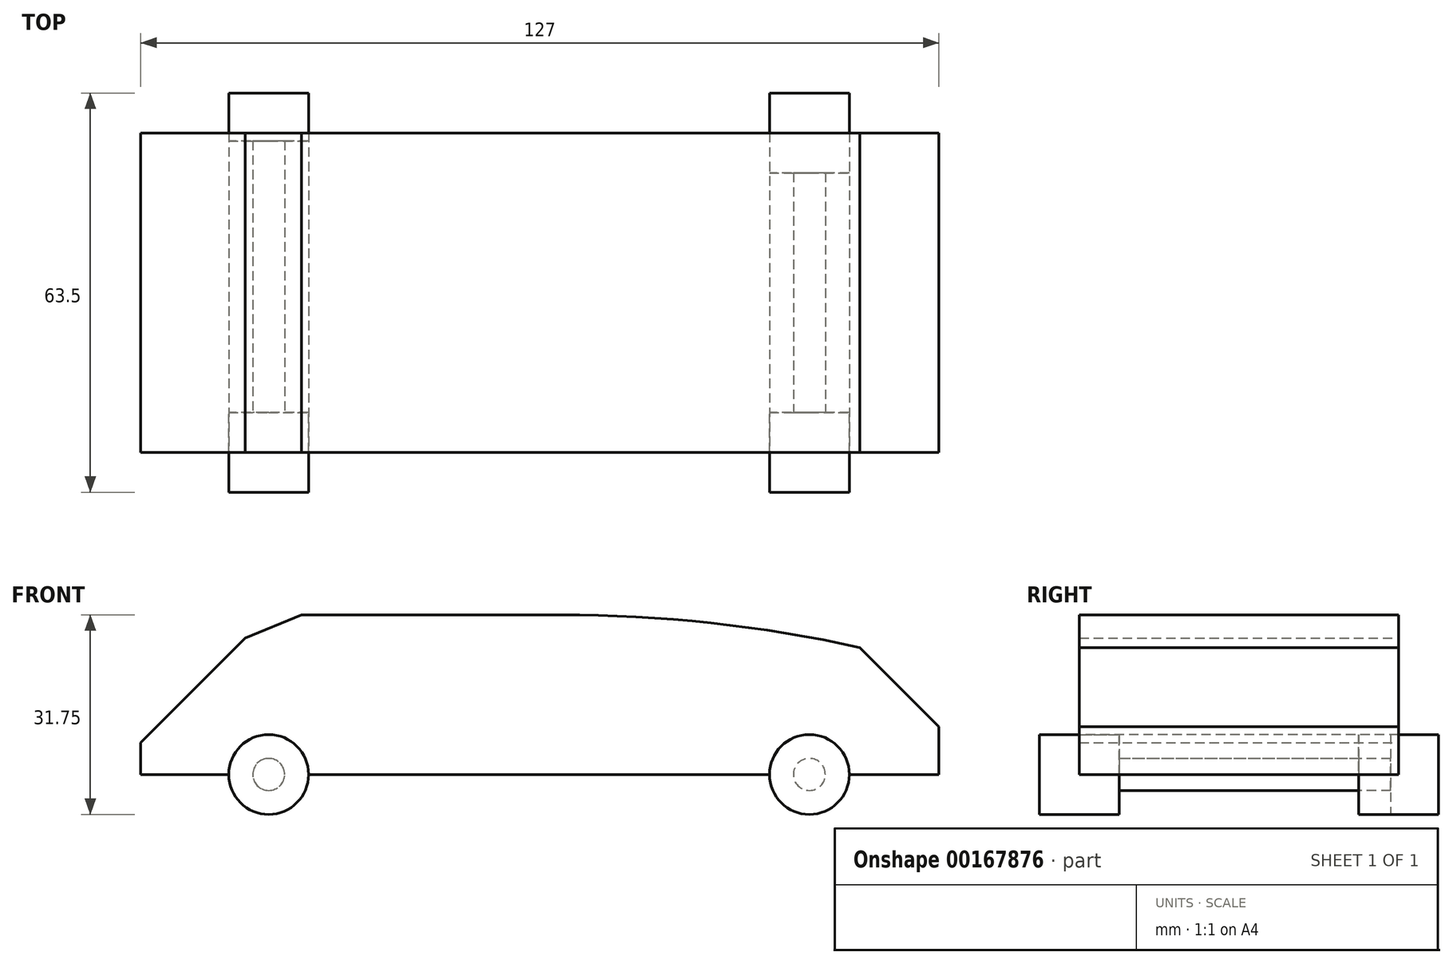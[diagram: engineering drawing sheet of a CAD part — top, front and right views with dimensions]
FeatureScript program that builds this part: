
annotation { "Feature Type Name" : "Feature", "Feature Type Description" : "" }
export const myFeature = defineFeature(function(context is Context, id is Id, definition is map)
    precondition{}
    {
        {
            var Q0;
            Q0=qCreatedBy(makeId("Top.planeOp"),FACE);
            var sketch = newSketch(context, id + "F0", { "sketchPlane" : qUnion([Q0])});
            skLineSegment(sketch, "E0.bottom", {"start": v(-59.82, 13.49) * mm, "end": v(67.18, 13.49) * mm});
            skLineSegment(sketch, "E0.top", {"start": v(-59.82, -37.31) * mm, "end": v(67.18, -37.31) * mm});
            skLineSegment(sketch, "E0.left", {"start": v(-59.82, 13.49) * mm, "end": v(-59.82, -37.31) * mm});
            skLineSegment(sketch, "E0.right", {"start": v(67.18, 13.49) * mm, "end": v(67.18, -37.31) * mm});
            skSolve(sketch);
        }
        {
            var Q0;
            Q0=makeQuery(id+"F0.imprint","IMPRINT",FACE,{"disambiguationData":[TD([[makeQuery(id+"F0.imprint","IMPRINT",EDGE,{"derivedFrom":sQuery(id+"F0.wireOp",EDGE,"E0.bottom")}),-1.0]])]});
            extrude(context, id + "F1", {"entities" : qUnion([Q0]), "depth" : 25.4 * mm});
        }
        {
            var Q0;
            Q0=makeQuery(id+"F1.opExtrude","CAP_EDGE",EDGE,{"disambiguationData":[OSD([sQuery(id+"F0.wireOp",EDGE,"E0.right")])],"isStart":false});
            chamfer(context, id + "F2", {"entities" : qUnion([Q0]), "width" : 17.78 * mm, "tangentPropagation" : true});
        }
        {
            var Q0;
            {var subQ0=sQuery(id+"F0.wireOp",EDGE,"E0.right");Q0=makeQuery(id+"F2.opChamfer","BLEND_EDGE",EDGE,{"blendedFrom":[makeQuery(id+"F1.opExtrude","CAP_EDGE",EDGE,{"disambiguationData":[OSD([subQ0])],"isStart":false}),makeQuery(id+"F1.opExtrude","CAP_FACE",FACE,{"disambiguationData":[OSD([sQuery(id+"F0.wireOp",EDGE,"E0.bottom"),sQuery(id+"F0.wireOp",EDGE,"E0.top"),sQuery(id+"F0.wireOp",EDGE,"E0.left"),subQ0])],"isStart":false})],"blendedInto":[makeQuery(id+"F1.opExtrude","CAP_FACE",FACE,{"disambiguationData":[OSD([sQuery(id+"F0.wireOp",EDGE,"E0.bottom"),sQuery(id+"F0.wireOp",EDGE,"E0.top"),sQuery(id+"F0.wireOp",EDGE,"E0.left"),subQ0])],"isStart":false})]});}
            chamfer(context, id + "F3", {"entities" : qUnion([Q0]), "width" : 17.78 * mm, "tangentPropagation" : true});
        }
        {
            var Q0;
            {var subQ0=sQuery(id+"F0.wireOp",EDGE,"E0.right");var subQ1=makeQuery(id+"F1.opExtrude","CAP_FACE",FACE,{"disambiguationData":[OSD([sQuery(id+"F0.wireOp",EDGE,"E0.bottom"),sQuery(id+"F0.wireOp",EDGE,"E0.top"),sQuery(id+"F0.wireOp",EDGE,"E0.left"),subQ0])],"isStart":false});Q0=makeQuery(id+"F3.opChamfer","BLEND_EDGE",EDGE,{"blendedFrom":[makeQuery(id+"F2.opChamfer","BLEND_EDGE",EDGE,{"blendedFrom":[makeQuery(id+"F1.opExtrude","CAP_EDGE",EDGE,{"disambiguationData":[OSD([subQ0])],"isStart":false}),subQ1],"blendedInto":[subQ1]}),subQ1],"blendedInto":[subQ1]});}
            fillet(context, id + "F4", {"entities" : qUnion([Q0]), "radius" : 220.4 * mm, "tangentPropagation" : true, "allowEdgeOverflow" : false});
        }
        {
            var Q0;
            Q0=makeQuery(id+"F1.opExtrude","CAP_EDGE",EDGE,{"disambiguationData":[OSD([sQuery(id+"F0.wireOp",EDGE,"E0.left")])],"isStart":false});
            chamfer(context, id + "F5", {"entities" : qUnion([Q0]), "width" : 20.32 * mm, "tangentPropagation" : true});
        }
        {
            var Q0;
            {var subQ0=sQuery(id+"F0.wireOp",EDGE,"E0.left");Q0=makeQuery(id+"F5.opChamfer","BLEND_EDGE",EDGE,{"blendedFrom":[makeQuery(id+"F1.opExtrude","CAP_EDGE",EDGE,{"disambiguationData":[OSD([subQ0])],"isStart":false}),makeQuery(id+"F1.opExtrude","CAP_FACE",FACE,{"disambiguationData":[OSD([sQuery(id+"F0.wireOp",EDGE,"E0.bottom"),sQuery(id+"F0.wireOp",EDGE,"E0.top"),subQ0,sQuery(id+"F0.wireOp",EDGE,"E0.right")])],"isStart":false})],"blendedInto":[makeQuery(id+"F1.opExtrude","CAP_FACE",FACE,{"disambiguationData":[OSD([sQuery(id+"F0.wireOp",EDGE,"E0.bottom"),sQuery(id+"F0.wireOp",EDGE,"E0.top"),subQ0,sQuery(id+"F0.wireOp",EDGE,"E0.right")])],"isStart":false})]});}
            chamfer(context, id + "F6", {"entities" : qUnion([Q0]), "width" : 12.7 * mm, "tangentPropagation" : true});
        }
        {
            var Q0;
            Q0=makeQuery(id+"F1.opExtrude","SWEPT_FACE",FACE,{"disambiguationData":[OSD([sQuery(id+"F0.wireOp",EDGE,"E0.top")])]});
            var sketch = newSketch(context, id + "F7", { "sketchPlane" : qUnion([Q0])});
            skCircle(sketch, "E1", {"center": v(-39.47, 0) * mm, "radius": 6.35 * mm});
            skCircle(sketch, "E2", {"center": v(46.57, 0) * mm, "radius": 6.35 * mm});
            skSolve(sketch);
        }
        {
            var Q0;
            Q0=makeQuery(id+"F1.opExtrude","SWEPT_FACE",FACE,{"disambiguationData":[OSD([sQuery(id+"F0.wireOp",EDGE,"E0.bottom")])]});
            var sketch = newSketch(context, id + "F8", { "sketchPlane" : qUnion([Q0])});
            skCircle(sketch, "E3.0", {"center": v(-46.57, 0) * mm, "radius": 6.35 * mm});
            skCircle(sketch, "E3.1", {"center": v(39.47, 0) * mm, "radius": 6.35 * mm});
            skCircle(sketch, "E4", {"center": v(-46.57, 0) * mm, "radius": 7.62 * mm});
            skCircle(sketch, "E5", {"center": v(39.47, 0) * mm, "radius": 7.62 * mm});
            skSolve(sketch);
        }
        {
            var Q0;
            {var subQ0=sQuery(id+"F8.wireOp",EDGE,"E3.0");var subQ1=makeQuery(id+"F1.opExtrude","CAP_EDGE",EDGE,{"disambiguationData":[OSD([sQuery(id+"F0.wireOp",EDGE,"E0.bottom")])],"isStart":true});var subQ2=makeQuery(id+"F8.imprint","INTERSECT",VERTEX,{"disambiguationData":[OD(0.0)],"derivedFrom":[subQ1,subQ0]});Q0=makeQuery(id+"F8.imprint","IMPRINT",FACE,{"disambiguationData":[TD([[makeQuery(id+"F8.imprint","IMPRINT",EDGE,{"disambiguationData":[TD([[subQ2,-1.0]])],"derivedFrom":subQ0}),1.0]])]});}
            var Q1;
            {var subQ0=sQuery(id+"F8.wireOp",EDGE,"E3.0");var subQ1=makeQuery(id+"F1.opExtrude","CAP_EDGE",EDGE,{"disambiguationData":[OSD([sQuery(id+"F0.wireOp",EDGE,"E0.bottom")])],"isStart":true});var subQ2=makeQuery(id+"F8.imprint","INTERSECT",VERTEX,{"disambiguationData":[OD(0.0)],"derivedFrom":[subQ1,subQ0]});Q1=makeQuery(id+"F8.imprint","IMPRINT",FACE,{"disambiguationData":[TD([[makeQuery(id+"F8.imprint","IMPRINT",EDGE,{"disambiguationData":[TD([[subQ2,-1.0]])],"derivedFrom":subQ0}),-1.0]])]});}
            var Q2;
            {var subQ0=sQuery(id+"F8.wireOp",EDGE,"E3.1");var subQ1=makeQuery(id+"F1.opExtrude","CAP_EDGE",EDGE,{"disambiguationData":[OSD([sQuery(id+"F0.wireOp",EDGE,"E0.bottom")])],"isStart":true});var subQ2=makeQuery(id+"F8.imprint","INTERSECT",VERTEX,{"disambiguationData":[OD(0.0)],"derivedFrom":[subQ1,subQ0]});Q2=makeQuery(id+"F8.imprint","IMPRINT",FACE,{"disambiguationData":[TD([[makeQuery(id+"F8.imprint","IMPRINT",EDGE,{"disambiguationData":[TD([[subQ2,1.0]])],"derivedFrom":subQ0}),-1.0]])]});}
            var Q3;
            {var subQ0=sQuery(id+"F8.wireOp",EDGE,"E3.1");var subQ1=makeQuery(id+"F1.opExtrude","CAP_EDGE",EDGE,{"disambiguationData":[OSD([sQuery(id+"F0.wireOp",EDGE,"E0.bottom")])],"isStart":true});var subQ2=makeQuery(id+"F8.imprint","INTERSECT",VERTEX,{"disambiguationData":[OD(0.0)],"derivedFrom":[subQ1,subQ0]});Q3=makeQuery(id+"F8.imprint","IMPRINT",FACE,{"disambiguationData":[TD([[makeQuery(id+"F8.imprint","IMPRINT",EDGE,{"disambiguationData":[TD([[subQ2,1.0]])],"derivedFrom":subQ0}),1.0]])]});}
            extrude(context, id + "F9", {"entities" : qUnion([Q0, Q1, Q2, Q3]), "operationType" : NewBodyOperationType.REMOVE, "oppositeDirection" : true, "depth" : 64 * mm});
        }
        {
            var Q0;
            {var subQ0=sQuery(id+"F7.wireOp",EDGE,"E1");var subQ1=makeQuery(id+"F1.opExtrude","CAP_EDGE",EDGE,{"disambiguationData":[OSD([sQuery(id+"F0.wireOp",EDGE,"E0.top")])],"isStart":true});var subQ2=makeQuery(id+"F7.imprint","INTERSECT",VERTEX,{"disambiguationData":[OD(0.0)],"derivedFrom":[subQ1,subQ0]});Q0=makeQuery(id+"F7.imprint","IMPRINT",FACE,{"disambiguationData":[TD([[makeQuery(id+"F7.imprint","IMPRINT",EDGE,{"disambiguationData":[TD([[subQ2,1.0]])],"derivedFrom":subQ0}),1.0]])]});}
            extrude(context, id + "F10", {"entities" : qUnion([Q0]), "operationType" : NewBodyOperationType.REMOVE, "oppositeDirection" : true, "depth" : 80.26 * mm});
        }
        {
            var Q0;
            {var subQ0=sQuery(id+"F7.wireOp",EDGE,"E1");var subQ1=makeQuery(id+"F1.opExtrude","CAP_EDGE",EDGE,{"disambiguationData":[OSD([sQuery(id+"F0.wireOp",EDGE,"E0.top")])],"isStart":true});var subQ2=makeQuery(id+"F7.imprint","INTERSECT",VERTEX,{"disambiguationData":[OD(0.0)],"derivedFrom":[subQ1,subQ0]});Q0=makeQuery(id+"F7.imprint","IMPRINT",FACE,{"disambiguationData":[TD([[makeQuery(id+"F7.imprint","IMPRINT",EDGE,{"disambiguationData":[TD([[subQ2,-1.0]])],"derivedFrom":subQ0}),1.0]])]});}
            var Q1;
            {var subQ0=sQuery(id+"F7.wireOp",EDGE,"E1");var subQ1=makeQuery(id+"F1.opExtrude","CAP_EDGE",EDGE,{"disambiguationData":[OSD([sQuery(id+"F0.wireOp",EDGE,"E0.top")])],"isStart":true});var subQ2=makeQuery(id+"F7.imprint","INTERSECT",VERTEX,{"disambiguationData":[OD(0.0)],"derivedFrom":[subQ1,subQ0]});Q1=makeQuery(id+"F7.imprint","IMPRINT",FACE,{"disambiguationData":[TD([[makeQuery(id+"F7.imprint","IMPRINT",EDGE,{"disambiguationData":[TD([[subQ2,1.0]])],"derivedFrom":subQ0}),1.0]])]});}
            extrude(context, id + "F11", {"entities" : qUnion([Q0, Q1]), "endBound" : BoundingType.SYMMETRIC, "depth" : 12.7 * mm});
        }
        {
            var Q0;
            Q0=makeQuery(id+"F11.opExtrude","CAP_FACE",FACE,{"disambiguationData":[OSD([sQuery(id+"F7.wireOp",EDGE,"E1")])],"isStart":true});
            var sketch = newSketch(context, id + "F12", { "sketchPlane" : qUnion([Q0])});
            skCircle(sketch, "E6", {"center": v(39.47, 0) * mm, "radius": 2.54 * mm});
            skSolve(sketch);
        }
        {
            var Q0;
            Q0 = qSketchRegion(id + "F12", true);
            extrude(context, id + "F13", {"entities" : qUnion([Q0]), "operationType" : NewBodyOperationType.REMOVE, "oppositeDirection" : true, "depth" : 5.08 * mm});
        }
        {
            var Q0;
            Q0=makeQuery(id+"F13.boolean.opBoolean","COPY",FACE,{"derivedFrom":makeQuery(id+"F13.opExtrude","CAP_FACE",FACE,{"disambiguationData":[OSD([sQuery(id+"F12.wireOp",EDGE,"E6")])],"isStart":false})});
            var sketch = newSketch(context, id + "F14", { "sketchPlane" : qUnion([Q0])});
            skCircle(sketch, "E7.0", {"center": v(39.47, 0) * mm, "radius": 2.54 * mm});
            skSolve(sketch);
        }
        {
            var Q0;
            {var subQ0=sQuery(id+"F7.wireOp",EDGE,"E2");var subQ1=makeQuery(id+"F1.opExtrude","CAP_EDGE",EDGE,{"disambiguationData":[OSD([sQuery(id+"F0.wireOp",EDGE,"E0.top")])],"isStart":true});var subQ2=makeQuery(id+"F7.imprint","INTERSECT",VERTEX,{"disambiguationData":[OD(0.0)],"derivedFrom":[subQ1,subQ0]});Q0=makeQuery(id+"F7.imprint","IMPRINT",FACE,{"disambiguationData":[TD([[makeQuery(id+"F7.imprint","IMPRINT",EDGE,{"disambiguationData":[TD([[subQ2,-1.0]])],"derivedFrom":subQ0}),1.0]])]});}
            extrude(context, id + "F15", {"entities" : qUnion([Q0]), "operationType" : NewBodyOperationType.REMOVE, "oppositeDirection" : true, "depth" : 108.7 * mm});
        }
        {
            var Q0;
            {var subQ0=sQuery(id+"F7.wireOp",EDGE,"E2");var subQ1=makeQuery(id+"F1.opExtrude","CAP_EDGE",EDGE,{"disambiguationData":[OSD([sQuery(id+"F0.wireOp",EDGE,"E0.top")])],"isStart":true});var subQ2=makeQuery(id+"F7.imprint","INTERSECT",VERTEX,{"disambiguationData":[OD(0.0)],"derivedFrom":[subQ1,subQ0]});Q0=makeQuery(id+"F7.imprint","IMPRINT",FACE,{"disambiguationData":[TD([[makeQuery(id+"F7.imprint","IMPRINT",EDGE,{"disambiguationData":[TD([[subQ2,-1.0]])],"derivedFrom":subQ0}),1.0]])]});}
            var Q1;
            {var subQ0=sQuery(id+"F7.wireOp",EDGE,"E2");var subQ1=makeQuery(id+"F1.opExtrude","CAP_EDGE",EDGE,{"disambiguationData":[OSD([sQuery(id+"F0.wireOp",EDGE,"E0.top")])],"isStart":true});var subQ2=makeQuery(id+"F7.imprint","INTERSECT",VERTEX,{"disambiguationData":[OD(0.0)],"derivedFrom":[subQ1,subQ0]});Q1=makeQuery(id+"F7.imprint","IMPRINT",FACE,{"disambiguationData":[TD([[makeQuery(id+"F7.imprint","IMPRINT",EDGE,{"disambiguationData":[TD([[subQ2,1.0]])],"derivedFrom":subQ0}),1.0]])]});}
            extrude(context, id + "F16", {"entities" : qUnion([Q0, Q1]), "endBound" : BoundingType.SYMMETRIC, "depth" : 12.7 * mm});
        }
        {
            var Q0;
            Q0=makeQuery(id+"F16.opExtrude","CAP_FACE",FACE,{"disambiguationData":[OSD([sQuery(id+"F7.wireOp",EDGE,"E2")])],"isStart":true});
            var sketch = newSketch(context, id + "F17", { "sketchPlane" : qUnion([Q0])});
            skCircle(sketch, "E8", {"center": v(-46.57, 0) * mm, "radius": 2.54 * mm});
            skSolve(sketch);
        }
        {
            var Q0;
            Q0=makeQuery(id+"F17.imprint","IMPRINT",FACE,{"disambiguationData":[TD([[makeQuery(id+"F17.imprint","IMPRINT",EDGE,{"derivedFrom":sQuery(id+"F17.wireOp",EDGE,"E8")}),1.0]])]});
            extrude(context, id + "F18", {"entities" : qUnion([Q0]), "operationType" : NewBodyOperationType.REMOVE, "oppositeDirection" : true, "depth" : 5.08 * mm});
        }
        {
            var Q0;
            Q0=makeQuery(id+"F1.opExtrude","SWEPT_FACE",FACE,{"disambiguationData":[OSD([sQuery(id+"F0.wireOp",EDGE,"E0.bottom")])]});
            var sketch = newSketch(context, id + "F19", { "sketchPlane" : qUnion([Q0])});
            skCircle(sketch, "E9.0", {"center": v(-46.57, 0) * mm, "radius": 6.35 * mm});
            skCircle(sketch, "E9.1", {"center": v(-46.57, 0) * mm, "radius": 2.54 * mm});
            skCircle(sketch, "E9.2", {"center": v(39.47, 0) * mm, "radius": 6.35 * mm});
            skCircle(sketch, "E9.3", {"center": v(39.47, 0) * mm, "radius": 2.54 * mm});
            skSolve(sketch);
        }
        {
            var Q0;
            Q0=makeQuery(id+"F19.imprint","IMPRINT",FACE,{"disambiguationData":[TD([[makeQuery(id+"F19.imprint","IMPRINT",EDGE,{"derivedFrom":sQuery(id+"F19.wireOp",EDGE,"E9.1")}),-1.0]])]});
            var Q1;
            Q1=makeQuery(id+"F19.imprint","IMPRINT",FACE,{"disambiguationData":[TD([[makeQuery(id+"F19.imprint","IMPRINT",EDGE,{"derivedFrom":sQuery(id+"F19.wireOp",EDGE,"E9.3")}),-1.0]])]});
            var Q2;
            Q2=makeQuery(id+"F19.imprint","IMPRINT",FACE,{"disambiguationData":[TD([[makeQuery(id+"F19.imprint","IMPRINT",EDGE,{"derivedFrom":sQuery(id+"F19.wireOp",EDGE,"E9.3")}),1.0]])]});
            var Q3;
            Q3=makeQuery(id+"F19.imprint","IMPRINT",FACE,{"disambiguationData":[TD([[makeQuery(id+"F19.imprint","IMPRINT",EDGE,{"derivedFrom":sQuery(id+"F19.wireOp",EDGE,"E9.1")}),1.0]])]});
            extrude(context, id + "F20", {"entities" : qUnion([Q0, Q1, Q2, Q3]), "endBound" : BoundingType.SYMMETRIC, "depth" : 12.7 * mm});
        }
        {
            var Q0;
            Q0=makeQuery(id+"F20.opExtrude","CAP_FACE",FACE,{"disambiguationData":[OSD([sQuery(id+"F19.wireOp",EDGE,"E9.2")])],"isStart":true});
            var sketch = newSketch(context, id + "F21", { "sketchPlane" : qUnion([Q0])});
            skCircle(sketch, "E10.0", {"center": v(46.57, 0) * mm, "radius": 2.54 * mm});
            skCircle(sketch, "E10.1", {"center": v(-39.47, 0) * mm, "radius": 2.54 * mm});
            skSolve(sketch);
        }
        {
            var Q0;
            Q0=makeQuery(id+"F21.imprint","IMPRINT",FACE,{"disambiguationData":[TD([[makeQuery(id+"F21.imprint","IMPRINT",EDGE,{"derivedFrom":sQuery(id+"F21.wireOp",EDGE,"E10.1")}),-1.0]])]});
            var Q1;
            Q1=makeQuery(id+"F21.imprint","IMPRINT",FACE,{"disambiguationData":[TD([[makeQuery(id+"F21.imprint","IMPRINT",EDGE,{"derivedFrom":sQuery(id+"F21.wireOp",EDGE,"E10.0")}),-1.0]])]});
            extrude(context, id + "F22", {"entities" : qUnion([Q0, Q1]), "operationType" : NewBodyOperationType.REMOVE, "oppositeDirection" : true, "depth" : 5.08 * mm});
        }
        {
            var Q0;
            Q0=makeQuery(id+"F13.boolean.opBoolean","COPY",FACE,{"derivedFrom":makeQuery(id+"F13.opExtrude","CAP_FACE",FACE,{"disambiguationData":[OSD([sQuery(id+"F12.wireOp",EDGE,"E6")])],"isStart":false})});
            var Q1;
            Q1=makeQuery(id+"F18.boolean.opBoolean","COPY",FACE,{"derivedFrom":makeQuery(id+"F18.opExtrude","CAP_FACE",FACE,{"disambiguationData":[OSD([sQuery(id+"F17.wireOp",EDGE,"E8")])],"isStart":false})});
            var Q2;
            Q2=makeQuery(id+"F22.boolean.opBoolean","COPY",FACE,{"derivedFrom":makeQuery(id+"F22.opExtrude","CAP_FACE",FACE,{"disambiguationData":[OSD([sQuery(id+"F21.wireOp",EDGE,"E10.1")])],"isStart":false})});
            extrude(context, id + "F23", {"entities" : qUnion([Q0, Q1]), "operationType" : NewBodyOperationType.ADD, "endBound" : BoundingType.UP_TO_SURFACE, "endBoundEntityFace" : qUnion([Q2]), "depth" : 25.4 * mm});
        }
    });
